# Revit family: Haworth_Atwell_TandemSeating_Large
name_source: partatom
category: Furniture
revit_build: Autodesk Revit 2018 (Build: 20170223_1515(x64)
units: mm (PartAtom-declared; Revit-internal decimal feet)

## family parameters
Always vertical = Yes
Cut with Voids When Loaded = No
OmniClass Number = 23.40.20.00
OmniClass Title = General Furniture and Specialties
Room Calculation Point = No
Shared = No
Work Plane-Based = No

## types (2) — shared parameters
Actual Depth = 2' - 6"
Actual Height = 3' - 0"
Assembly Code = E2020200
Manufacturer = Haworth
Model = Haworth Atwell
Size = Verify Final Dim. w/ Haworth
Sustainability Info = https://www.haworth.com
URL = http://healthcare.haworth.com
URL - Product = https://healthcare.haworth.com
Version = 0
Warranty = https://www.haworth.com

## per-type parameters (varying)
| type | Actual Width | Description | Three Seat | Two Seat |
| HE902-T2LB - 56w | 4' - 8 1/4" | Tandem Seating - 2 Seat - Large Occupant | No | Yes |
| HE903-T3LB - 80w | 6' - 8" | Tandem Seating - 3 Seat - Large Occupant | Yes | No |

## geometry (parser evidence)
native form markers: Sweep x16
no freeform markers — native parametric forms only
